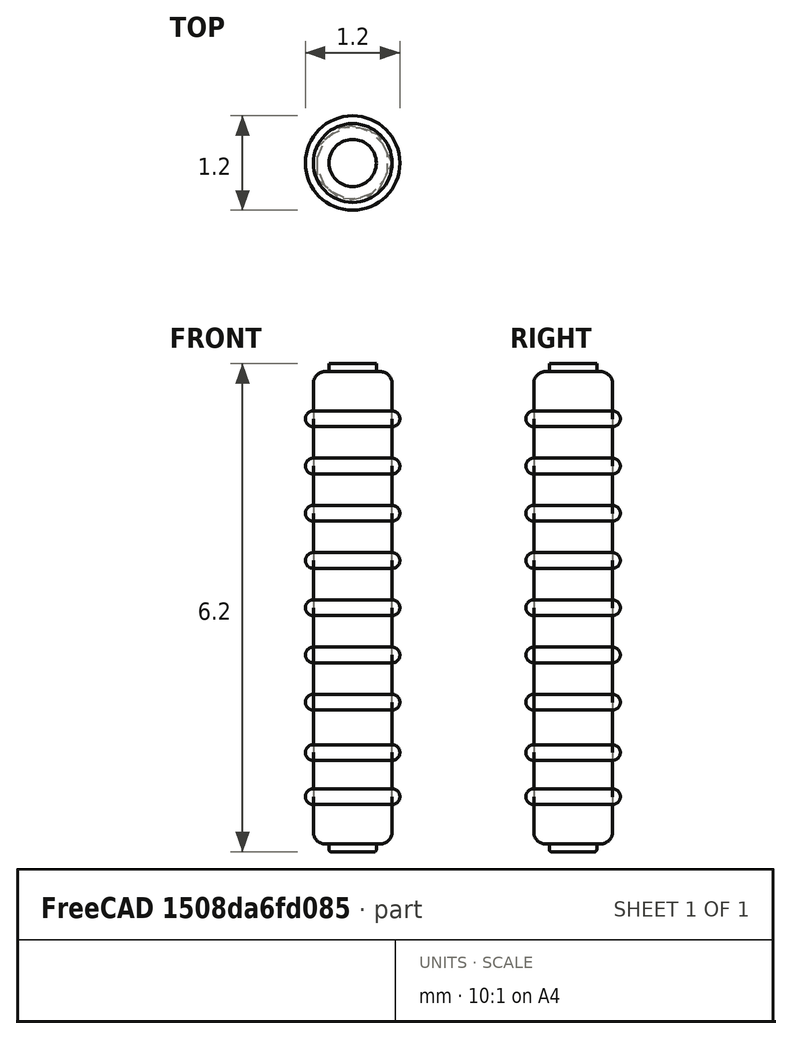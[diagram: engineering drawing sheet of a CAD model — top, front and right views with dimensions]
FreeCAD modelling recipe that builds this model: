
FCSTD DOCUMENT  (FreeCAD 0.16R6712 (Git))
Label: fixdigits
License: All rights reserved
LicenseURL: http://en.wikipedia.org/wiki/All_rights_reserved
objects: Part::Torus×9, Sketcher::SketchObject×3, PartDesign::Pad×3, PartDesign::Fillet×2, Part::MultiFuse×1, Mesh::Feature×1
note: 21 computed .brp shape members not serialized (recipe doc carries the construction recipe); baked Part::Feature solids carry a one-line shape summary decoded from their .brp

FEATURE [Sketcher::SketchObject] Sketch
  sketch-geometry (1):
    g0: Circle CenterX=0 CenterY=-0.4 CenterZ=0 NormalX=0 NormalY=0 NormalZ=1 Radius=0.5
  constraints (3):
    c: Radius(g0) = 0.5
    c: DistanceY(g-1,g0) = -0.4
    c: PointOnObject(g0,g-2)
FEATURE [PartDesign::Pad] Pad
  Length = 3
  Length2 = 3
  Sketch = -> Sketch
  Type = 4
FEATURE [PartDesign::Fillet] Fillet
  Base = -> Pad [Edge2,Edge3]
  Radius = 0.15
FEATURE [Sketcher::SketchObject] Sketch001
  Placement = pos=(0,0,3) rot=(0,0,1;0rad)
  Support = -> Fillet [Face5]
  sketch-geometry (1):
    g0: Circle CenterX=0 CenterY=-0.4 CenterZ=0 NormalX=0 NormalY=0 NormalZ=1 Radius=0.3
  constraints (3):
    c: PointOnObject(g0,g-2)
    c: DistanceY(g-1,g0) = -0.4
    c: Radius(g0) = 0.3
FEATURE [PartDesign::Pad] Pad001
  Length = 0.1
  Length2 = 100
  Sketch = -> Sketch001
  Type = 0
FEATURE [Sketcher::SketchObject] Sketch002
  Placement = pos=(0,0,-3) rot=(1,0,0;3.14159rad)
  Support = -> Pad001 [Face7]
  sketch-geometry (1):
    g0: Circle CenterX=0 CenterY=0.4 CenterZ=0 NormalX=0 NormalY=0 NormalZ=1 Radius=0.3
  constraints (3):
    c: PointOnObject(g0,g-2)
    c: Radius(g0) = 0.3
    c: DistanceY(g-1,g0) = 0.4
FEATURE [PartDesign::Pad] Pad002
  Length = 0.1
  Length2 = 100
  Sketch = -> Sketch002
  Type = 0
FEATURE [PartDesign::Fillet] Fillet001
  Base = -> Pad002 [Edge1,Edge2,Edge13,Edge11]
  Radius = 0.025
FEATURE [Part::Torus] Torus
  Angle1 = -180
  Angle2 = 180
  Angle3 = 360
  Placement = pos=(0,-0.4,0.6) rot=(0,0,1;0rad)
  Radius1 = 0.5
  Radius2 = 0.1
FEATURE [Part::Torus] Torus001
  Angle1 = -180
  Angle2 = 180
  Angle3 = 360
  Placement = pos=(0,-0.4,1.2) rot=(0,0,1;0rad)
  Radius1 = 0.5
  Radius2 = 0.1
FEATURE [Part::Torus] Torus002
  Angle1 = -180
  Angle2 = 180
  Angle3 = 360
  Placement = pos=(0,-0.4,0) rot=(0,0,1;0rad)
  Radius1 = 0.5
  Radius2 = 0.1
FEATURE [Part::Torus] Torus003
  Angle1 = -180
  Angle2 = 180
  Angle3 = 360
  Placement = pos=(0,-0.4,1.8) rot=(0,0,1;0rad)
  Radius1 = 0.5
  Radius2 = 0.1
FEATURE [Part::Torus] Torus004
  Angle1 = -180
  Angle2 = 180
  Angle3 = 360
  Placement = pos=(0,-0.4,-0.6) rot=(0,0,1;0rad)
  Radius1 = 0.5
  Radius2 = 0.1
FEATURE [Part::Torus] Torus005
  Angle1 = -180
  Angle2 = 180
  Angle3 = 360
  Placement = pos=(0,-0.4,-1.2) rot=(0,0,1;0rad)
  Radius1 = 0.5
  Radius2 = 0.1
FEATURE [Part::Torus] Torus006
  Angle1 = -180
  Angle2 = 180
  Angle3 = 360
  Placement = pos=(0,-0.4,-1.84) rot=(0,0,1;0rad)
  Radius1 = 0.5
  Radius2 = 0.1
FEATURE [Part::Torus] Torus007
  Angle1 = -180
  Angle2 = 180
  Angle3 = 360
  Placement = pos=(0,-0.4,-2.4) rot=(0,0,1;0rad)
  Radius1 = 0.5
  Radius2 = 0.1
FEATURE [Part::Torus] Torus008
  Angle1 = -180
  Angle2 = 180
  Angle3 = 360
  Placement = pos=(0,-0.4,2.4) rot=(0,0,1;0rad)
  Radius1 = 0.5
  Radius2 = 0.1
FEATURE [Part::MultiFuse] Fusion
  Shapes = -> [Fillet001,Torus007,Torus006,Torus005,Torus004,Torus002,Torus,Torus001,Torus003,Torus008]
FEATURE [Mesh::Feature] Mesh  label="Fusion (Meshed)"
